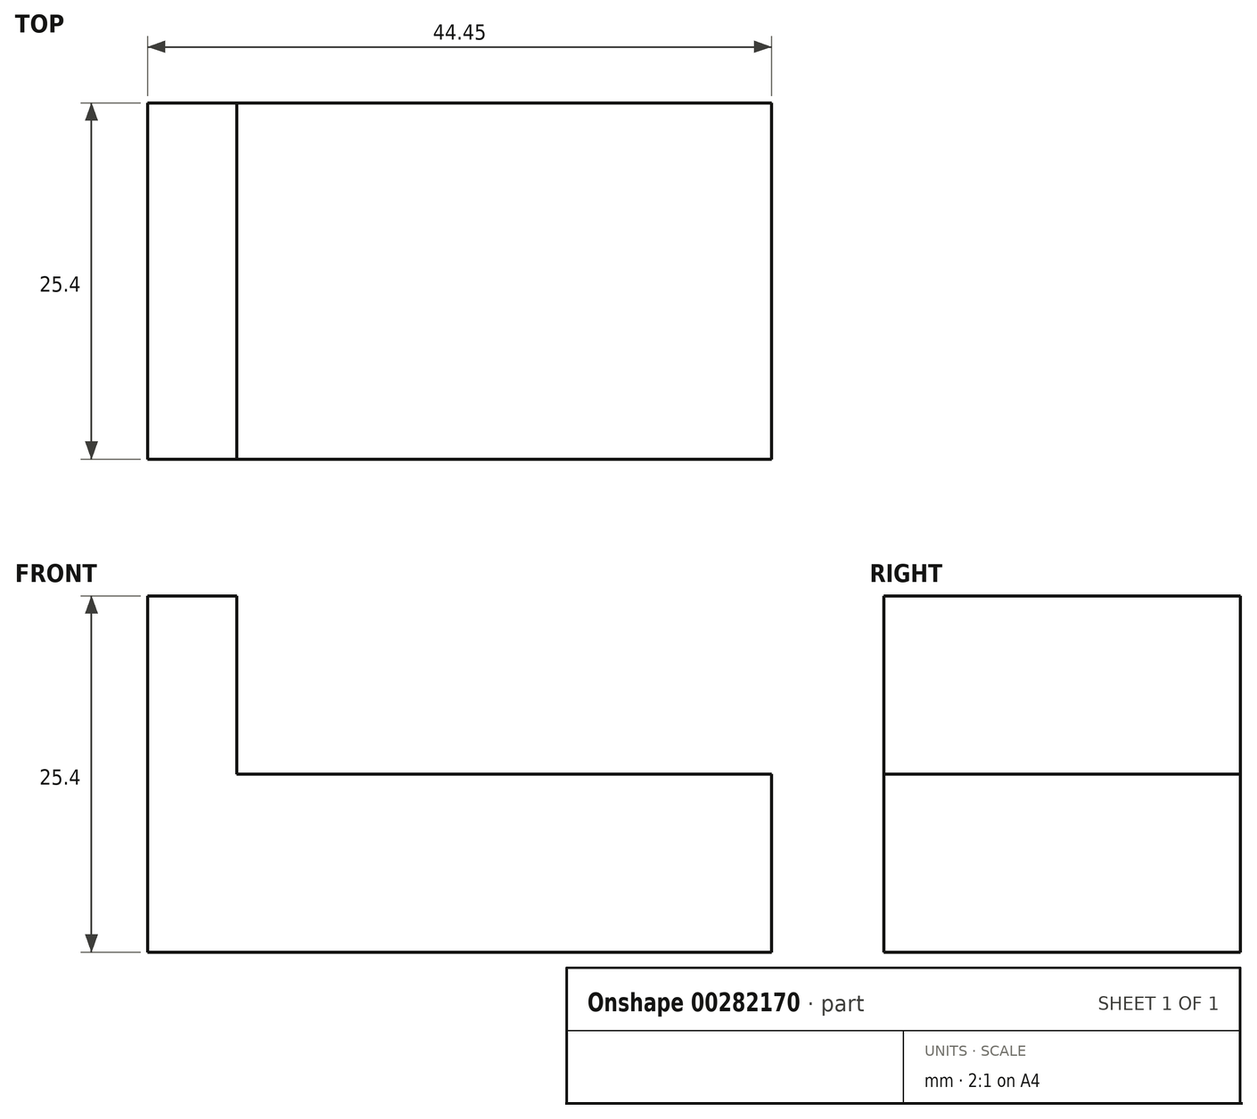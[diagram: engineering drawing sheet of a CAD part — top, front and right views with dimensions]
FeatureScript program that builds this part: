
annotation { "Feature Type Name" : "Feature", "Feature Type Description" : "" }
export const myFeature = defineFeature(function(context is Context, id is Id, definition is map)
    precondition{}
    {
        {
            var Q0;
            Q0=qCreatedBy(makeId("Front.planeOp"),FACE);
            var sketch = newSketch(context, id + "F0", { "sketchPlane" : qUnion([Q0])});
            skLineSegment(sketch, "E0", {"start": v(0, 0) * mm, "end": v(0, 25.4) * mm});
            skLineSegment(sketch, "E1", {"start": v(0, 25.4) * mm, "end": v(6.35, 25.4) * mm});
            skLineSegment(sketch, "E2", {"start": v(6.35, 25.4) * mm, "end": v(6.35, 12.7) * mm});
            skLineSegment(sketch, "E3", {"start": v(6.35, 12.7) * mm, "end": v(44.45, 12.7) * mm});
            skLineSegment(sketch, "E4", {"start": v(44.45, 12.7) * mm, "end": v(44.45, 0) * mm});
            skLineSegment(sketch, "E5", {"start": v(44.45, 0) * mm, "end": v(0, 0) * mm});
            skSolve(sketch);
        }
        {
            var Q0;
            Q0=makeQuery(id+"F0.imprint","IMPRINT",FACE,{"disambiguationData":[TD([[makeQuery(id+"F0.imprint","IMPRINT",EDGE,{"derivedFrom":sQuery(id+"F0.wireOp",EDGE,"E0")}),-1.0]])]});
            extrude(context, id + "F1", {"entities" : qUnion([Q0]), "depth" : 25.4 * mm});
        }
    });
